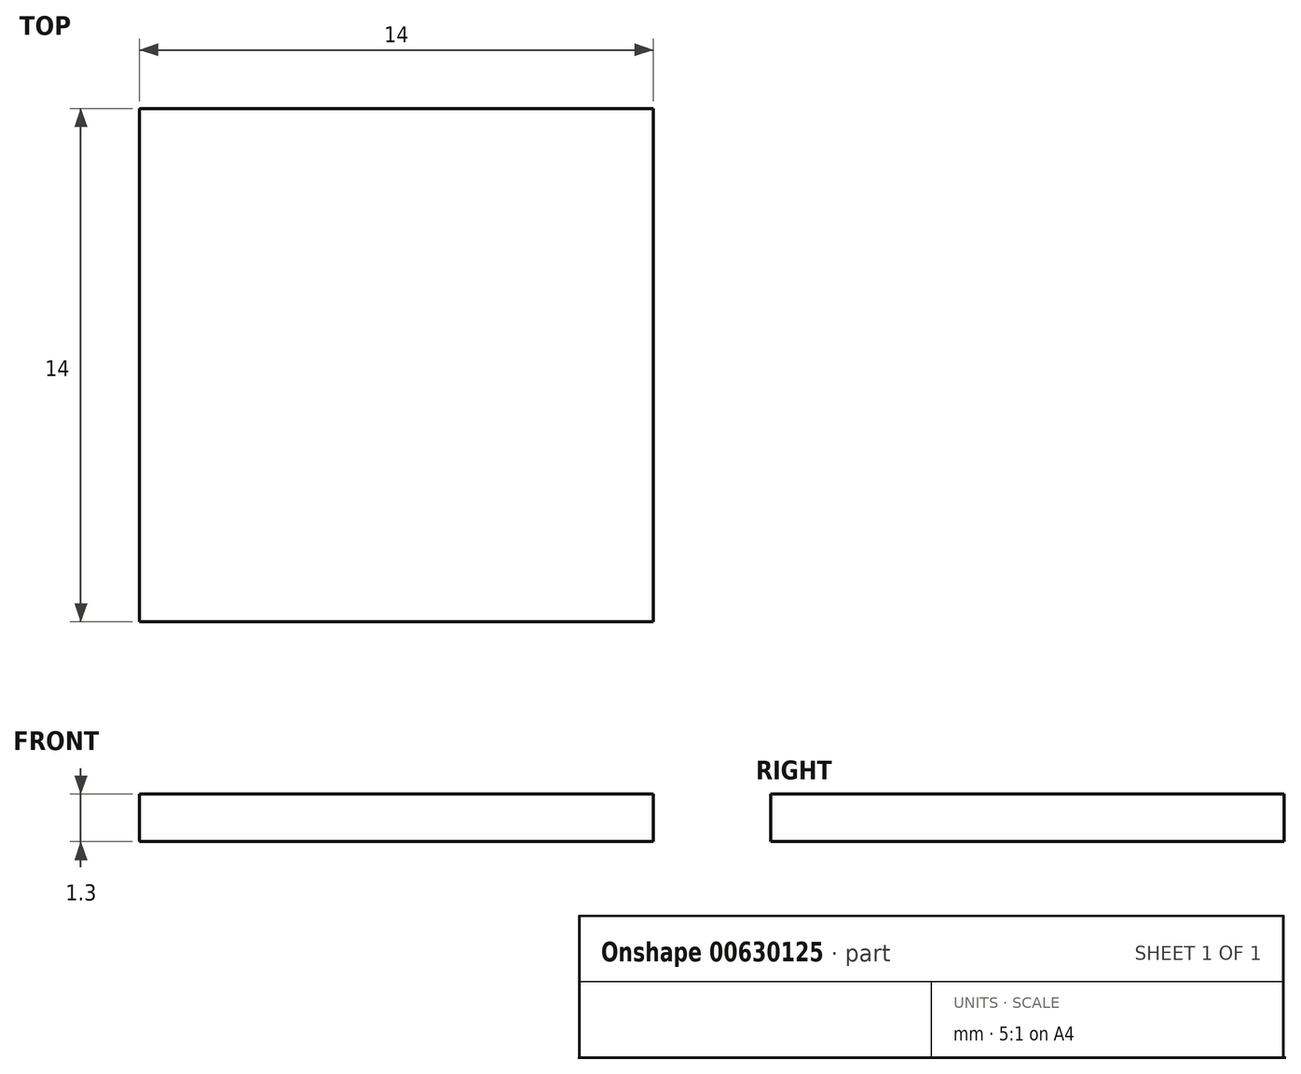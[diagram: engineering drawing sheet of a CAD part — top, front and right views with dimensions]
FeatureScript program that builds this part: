
annotation { "Feature Type Name" : "Feature", "Feature Type Description" : "" }
export const myFeature = defineFeature(function(context is Context, id is Id, definition is map)
    precondition{}
    {
        {
            var Q0;
            Q0=qCreatedBy(makeId("Top.planeOp"),FACE);
            var sketch = newSketch(context, id + "F0", { "sketchPlane" : qUnion([Q0])});
            skLineSegment(sketch, "E0.bottom", {"start": v(0, 0) * mm, "end": v(14, 0) * mm});
            skLineSegment(sketch, "E0.top", {"start": v(0, 14) * mm, "end": v(14, 14) * mm});
            skLineSegment(sketch, "E0.left", {"start": v(0, 0) * mm, "end": v(0, 14) * mm});
            skLineSegment(sketch, "E0.right", {"start": v(14, 0) * mm, "end": v(14, 14) * mm});
            skSolve(sketch);
        }
        {
            var Q0;
            Q0=qSketchRegion(id+"F0",true);
            extrude(context, id + "F1", {"entities" : qUnion([Q0]), "depth" : 1.3 * mm});
        }
    });
